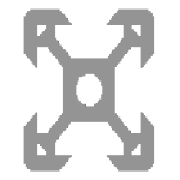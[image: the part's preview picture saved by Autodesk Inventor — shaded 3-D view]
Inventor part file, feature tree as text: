
AUTODESK INVENTOR PART (.ipt)
format: ipt  version: 2019 (Build 230136000, 136)  size: 200,704 bytes
history: native  units: mm
features: other x3, sketch x3, plane x1
ambient origin geometry x8: Origin, YZ Plane, XZ Plane, XY Plane, X Axis, Y Axis, Z Axis, Center Point
bodies: Solid1 (feature_tree), Body (feature_tree)
feature tree (7):
  other  "Driven Length"
  other  "Start Plane"
  other  "End Plane"
  sketch  "Sketch1"  dims[d2=4.2mm]
  sketch  "Sketch4"  dims[d3=1.5mm]
  plane  "Work Plane4"
  sketch  "Sketch5"  dims[d4=1.64mm d5=1.8mm d6=5.68mm d7=1.8mm d9=1.5mm d12=-0.0mm d13=550.0mm d14=0.13mm d15=0.0mm d18=90.0deg d17=550.0mm]
